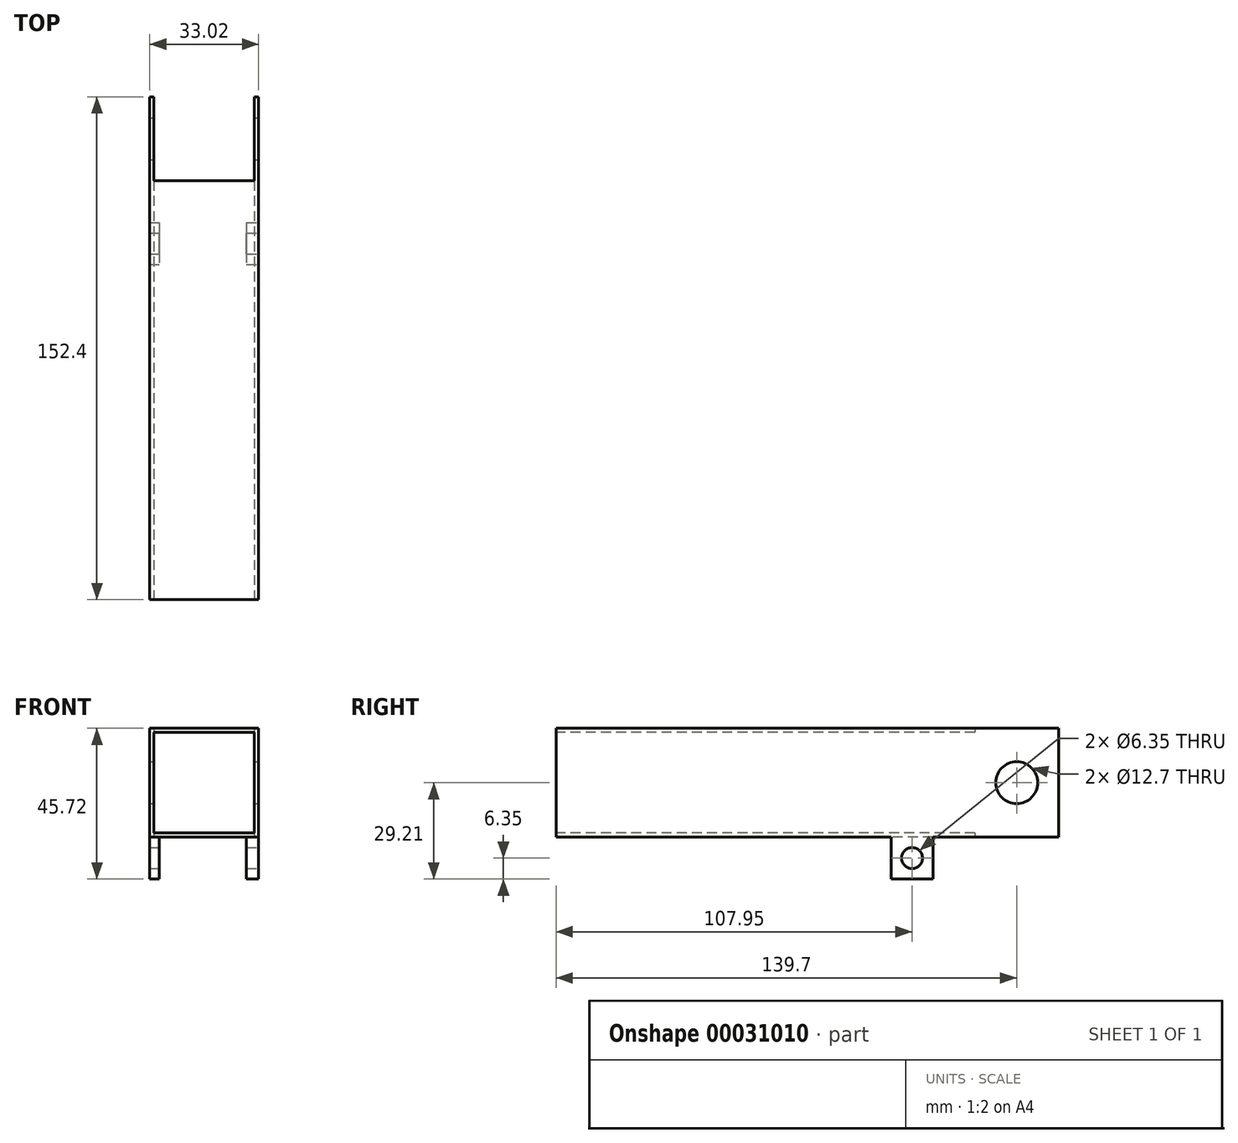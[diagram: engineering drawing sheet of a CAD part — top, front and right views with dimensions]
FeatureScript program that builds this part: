
annotation { "Feature Type Name" : "Feature", "Feature Type Description" : "" }
export const myFeature = defineFeature(function(context is Context, id is Id, definition is map)
    precondition{}
    {
        {
            var Q0;
            Q0=qCreatedBy(makeId("Front.planeOp"),FACE);
            var sketch = newSketch(context, id + "F0", { "sketchPlane" : qUnion([Q0])});
            skLineSegment(sketch, "E0.rect.bottom", {"start": v(16.51, 16.51) * mm, "end": v(-16.51, 16.51) * mm});
            skLineSegment(sketch, "E0.rect.top", {"start": v(16.51, -16.51) * mm, "end": v(-16.51, -16.51) * mm});
            skLineSegment(sketch, "E0.rect.left", {"start": v(16.51, 16.51) * mm, "end": v(16.51, -16.51) * mm});
            skLineSegment(sketch, "E0.rect.right", {"start": v(-16.51, 16.51) * mm, "end": v(-16.51, -16.51) * mm});
            skPoint(sketch, "E0.rect.middle", {"position": v(0, 0) * mm});
            skSolve(sketch);
        }
        {
            var Q0;
            Q0=makeQuery(id+"F0.imprint","IMPRINT",FACE,{"disambiguationData":[TD([[makeQuery(id+"F0.imprint","IMPRINT",EDGE,{"derivedFrom":sQuery(id+"F0.wireOp",EDGE,"E0.rect.bottom")}),1.0]])]});
            extrude(context, id + "F1", {"entities" : qUnion([Q0]), "depth" : 127 * mm});
        }
        {
            var Q0;
            Q0=makeQuery(id+"F1.opExtrude","CAP_FACE",FACE,{"disambiguationData":[OSD([sQuery(id+"F0.wireOp",EDGE,"E0.rect.bottom"),sQuery(id+"F0.wireOp",EDGE,"E0.rect.top"),sQuery(id+"F0.wireOp",EDGE,"E0.rect.left"),sQuery(id+"F0.wireOp",EDGE,"E0.rect.right")])],"isStart":false});
            var sketch = newSketch(context, id + "F2", { "sketchPlane" : qUnion([Q0])});
            skLineSegment(sketch, "E1.rect.bottom", {"start": v(15.24, 15.24) * mm, "end": v(-15.24, 15.24) * mm});
            skLineSegment(sketch, "E1.rect.top", {"start": v(15.24, -15.24) * mm, "end": v(-15.24, -15.24) * mm});
            skLineSegment(sketch, "E1.rect.left", {"start": v(15.24, 15.24) * mm, "end": v(15.24, -15.24) * mm});
            skLineSegment(sketch, "E1.rect.right", {"start": v(-15.24, 15.24) * mm, "end": v(-15.24, -15.24) * mm});
            skPoint(sketch, "E1.rect.middle", {"position": v(0, 0) * mm});
            skSolve(sketch);
        }
        {
            var Q0;
            Q0=makeQuery(id+"F2.imprint","IMPRINT",FACE,{"disambiguationData":[TD([[makeQuery(id+"F2.imprint","IMPRINT",EDGE,{"derivedFrom":sQuery(id+"F2.wireOp",EDGE,"E1.rect.bottom")}),1.0]])]});
            extrude(context, id + "F3", {"entities" : qUnion([Q0]), "operationType" : NewBodyOperationType.REMOVE, "oppositeDirection" : true, "depth" : 127 * mm});
        }
        {
            var Q0;
            Q0=makeQuery(id+"F1.opExtrude","SWEPT_FACE",FACE,{"disambiguationData":[OSD([sQuery(id+"F0.wireOp",EDGE,"E0.rect.left")])]});
            var sketch = newSketch(context, id + "F4", { "sketchPlane" : qUnion([Q0])});
            skLineSegment(sketch, "E2.bottom", {"start": v(0, 16.51) * mm, "end": v(25.4, 16.51) * mm});
            skLineSegment(sketch, "E2.top", {"start": v(0, -16.51) * mm, "end": v(25.4, -16.51) * mm});
            skLineSegment(sketch, "E2.left", {"start": v(0, 16.51) * mm, "end": v(0, -16.51) * mm});
            skLineSegment(sketch, "E2.right", {"start": v(25.4, 16.51) * mm, "end": v(25.4, -16.51) * mm});
            skCircle(sketch, "E3", {"center": v(12.7, 0) * mm, "radius": 6.35 * mm});
            skPoint(sketch, "E3.centerSnap0", {"position": v(12.7, -16.51) * mm});
            skSolve(sketch);
        }
        {
            var Q0;
            Q0=makeQuery(id+"F4.imprint","IMPRINT",FACE,{"disambiguationData":[TD([[makeQuery(id+"F4.imprint","IMPRINT",EDGE,{"derivedFrom":sQuery(id+"F4.wireOp",EDGE,"E2.bottom")}),-1.0]])]});
            extrude(context, id + "F5", {"entities" : qUnion([Q0]), "operationType" : NewBodyOperationType.ADD, "oppositeDirection" : true, "depth" : 33.02 * mm});
        }
        {
            var Q0;
            Q0=makeQuery(id+"F5.opExtrude","SWEPT_FACE",FACE,{"disambiguationData":[OSD([sQuery(id+"F4.wireOp",EDGE,"E2.right")])]});
            var sketch = newSketch(context, id + "F6", { "sketchPlane" : qUnion([Q0])});
            skLineSegment(sketch, "E4.rect.bottom", {"start": v(15.24, 16.51) * mm, "end": v(-15.24, 16.51) * mm});
            skLineSegment(sketch, "E4.rect.top", {"start": v(15.24, -16.51) * mm, "end": v(-15.24, -16.51) * mm});
            skLineSegment(sketch, "E4.rect.left", {"start": v(15.24, 16.51) * mm, "end": v(15.24, -16.51) * mm});
            skLineSegment(sketch, "E4.rect.right", {"start": v(-15.24, 16.51) * mm, "end": v(-15.24, -16.51) * mm});
            skPoint(sketch, "E4.rect.middle", {"position": v(0, 0) * mm});
            skSolve(sketch);
        }
        {
            var Q0;
            Q0=makeQuery(id+"F6.imprint","IMPRINT",FACE,{"disambiguationData":[TD([[makeQuery(id+"F6.imprint","IMPRINT",EDGE,{"derivedFrom":sQuery(id+"F6.wireOp",EDGE,"E4.rect.bottom")}),1.0]])]});
            extrude(context, id + "F7", {"entities" : qUnion([Q0]), "operationType" : NewBodyOperationType.REMOVE, "oppositeDirection" : true, "depth" : 25.4 * mm});
        }
        {
            var Q0;
            Q0=makeQuery(id+"F5.boolean.opBoolean","MERGE",FACE,{"derivedFrom":[makeQuery(id+"F1.opExtrude","SWEPT_FACE",FACE,{"disambiguationData":[OSD([sQuery(id+"F0.wireOp",EDGE,"E0.rect.left")])]}),makeQuery(id+"F5.opExtrude","CAP_FACE",FACE,{"disambiguationData":[OSD([sQuery(id+"F4.wireOp",EDGE,"E2.bottom"),sQuery(id+"F4.wireOp",EDGE,"E2.top"),sQuery(id+"F4.wireOp",EDGE,"E2.left"),sQuery(id+"F4.wireOp",EDGE,"E2.right"),sQuery(id+"F4.wireOp",EDGE,"E3")])],"isStart":true})]});
            var sketch = newSketch(context, id + "F8", { "sketchPlane" : qUnion([Q0])});
            skLineSegment(sketch, "E5", {"start": v(25.4, -16.51) * mm, "end": v(-12.7, -16.51) * mm});
            skLineSegment(sketch, "E6.bottom", {"start": v(-12.7, -16.51) * mm, "end": v(-25.4, -16.51) * mm});
            skLineSegment(sketch, "E6.top", {"start": v(-12.7, -29.21) * mm, "end": v(-25.4, -29.21) * mm});
            skLineSegment(sketch, "E6.left", {"start": v(-12.7, -16.51) * mm, "end": v(-12.7, -29.21) * mm});
            skLineSegment(sketch, "E6.right", {"start": v(-25.4, -16.51) * mm, "end": v(-25.4, -29.21) * mm});
            skCircle(sketch, "E7", {"center": v(-19.05, -22.86) * mm, "radius": 3.18 * mm});
            skPoint(sketch, "E7.centerSnap0", {"position": v(-12.7, -22.86) * mm});
            skPoint(sketch, "E7.centerSnap1", {"position": v(-19.05, -16.51) * mm});
            skSolve(sketch);
        }
        {
            var Q0;
            Q0=makeQuery(id+"F8.imprint","IMPRINT",FACE,{"disambiguationData":[TD([[makeQuery(id+"F8.imprint","IMPRINT",EDGE,{"derivedFrom":sQuery(id+"F8.wireOp",EDGE,"E6.bottom")}),-1.0]])]});
            extrude(context, id + "F9", {"entities" : qUnion([Q0]), "operationType" : NewBodyOperationType.ADD, "oppositeDirection" : true, "depth" : 33.02 * mm});
        }
        {
            var Q0;
            Q0=makeQuery(id+"F9.opExtrude","SWEPT_FACE",FACE,{"disambiguationData":[OSD([sQuery(id+"F8.wireOp",EDGE,"E6.top")])]});
            var sketch = newSketch(context, id + "F10", { "sketchPlane" : qUnion([Q0])});
            skLineSegment(sketch, "E8.bottom", {"start": v(-13.6, 12.7) * mm, "end": v(12.86, 12.7) * mm});
            skLineSegment(sketch, "E8.top", {"start": v(-13.6, 25.4) * mm, "end": v(12.86, 25.4) * mm});
            skLineSegment(sketch, "E8.left", {"start": v(-13.6, 12.7) * mm, "end": v(-13.6, 25.4) * mm});
            skLineSegment(sketch, "E8.right", {"start": v(12.86, 12.7) * mm, "end": v(12.86, 25.4) * mm});
            skLineSegment(sketch, "E9", {"start": v(-16.51, 25.4) * mm, "end": v(-13.6, 25.4) * mm});
            skLineSegment(sketch, "E10", {"start": v(12.86, 25.4) * mm, "end": v(16.51, 25.4) * mm});
            skSolve(sketch);
        }
        {
            var Q0;
            Q0=makeQuery(id+"F10.imprint","IMPRINT",FACE,{"disambiguationData":[TD([[makeQuery(id+"F10.imprint","IMPRINT",EDGE,{"derivedFrom":sQuery(id+"F10.wireOp",EDGE,"E8.bottom")}),1.0]])]});
            extrude(context, id + "F11", {"entities" : qUnion([Q0]), "operationType" : NewBodyOperationType.REMOVE, "oppositeDirection" : true, "depth" : 12.7 * mm});
        }
    });
